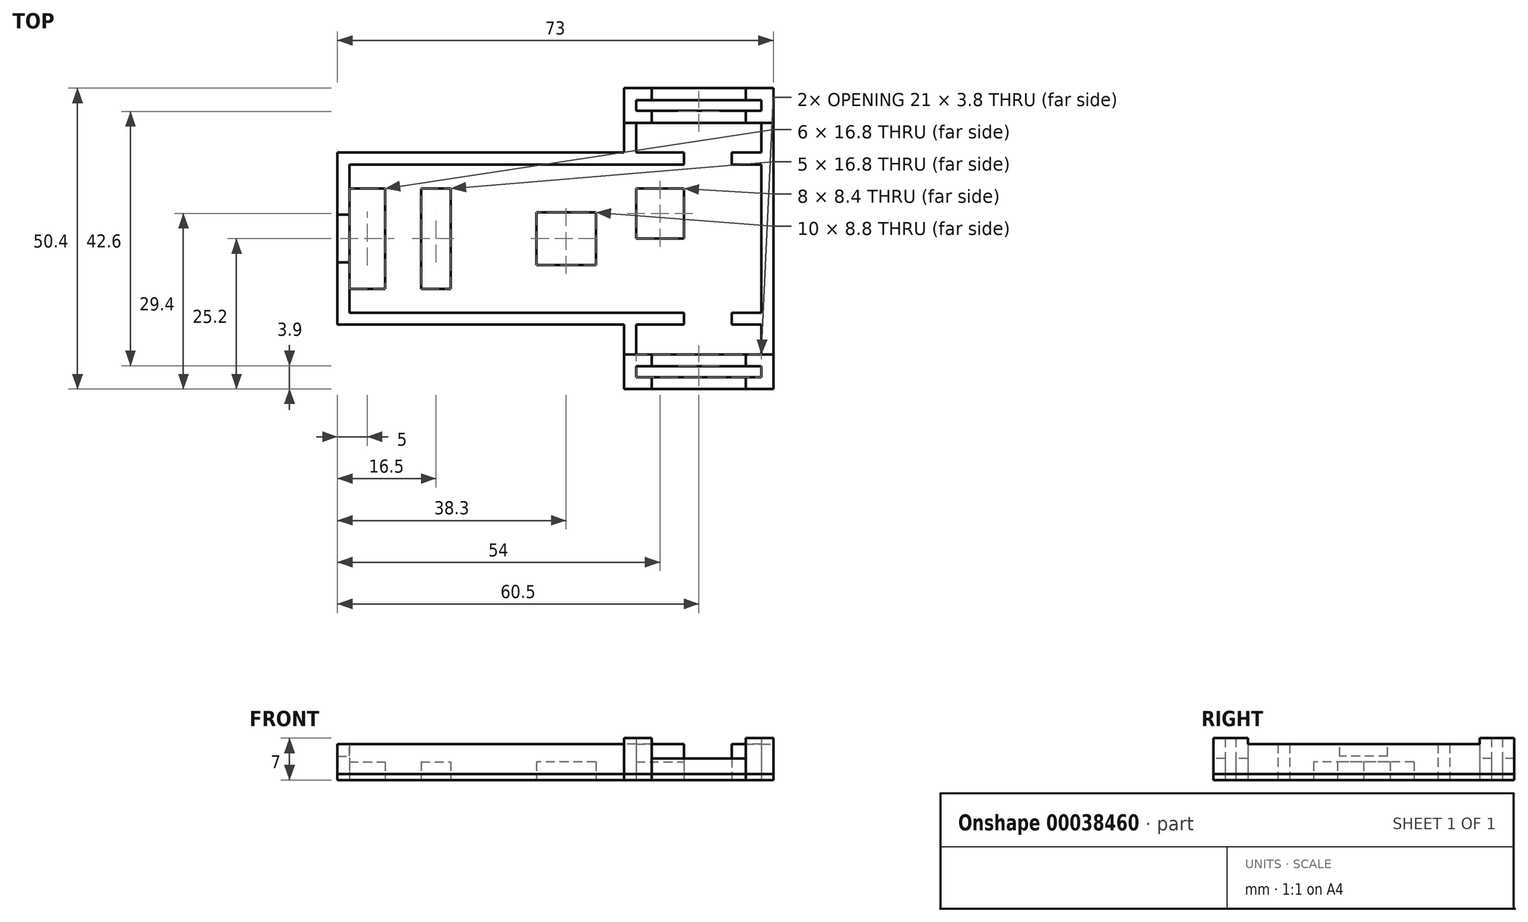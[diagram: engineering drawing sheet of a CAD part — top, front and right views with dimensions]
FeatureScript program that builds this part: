
annotation { "Feature Type Name" : "Feature", "Feature Type Description" : "" }
export const myFeature = defineFeature(function(context is Context, id is Id, definition is map)
    precondition{}
    {
        {
            var Q0;
            Q0=qCreatedBy(makeId("Top.planeOp"),FACE);
            var sketch = newSketch(context, id + "F0", { "sketchPlane" : qUnion([Q0])});
            skLineSegment(sketch, "E0.bottom", {"start": v(0, 0) * mm, "end": v(69, 0) * mm, "construction": true});
            skLineSegment(sketch, "E0.top", {"start": v(0, 24.8) * mm, "end": v(69, 24.8) * mm, "construction": true});
            skLineSegment(sketch, "E0.left", {"start": v(0, 0) * mm, "end": v(0, 24.8) * mm, "construction": true});
            skLineSegment(sketch, "E0.right", {"start": v(69, 0) * mm, "end": v(69, 24.8) * mm, "construction": true});
            skLineSegment(sketch, "E1.bottom", {"start": v(-2, 26.8) * mm, "end": v(71, 26.8) * mm, "construction": true});
            skLineSegment(sketch, "E1.top", {"start": v(-2, -2) * mm, "end": v(71, -2) * mm, "construction": true});
            skLineSegment(sketch, "E1.left", {"start": v(-2, 26.8) * mm, "end": v(-2, -2) * mm, "construction": true});
            skLineSegment(sketch, "E1.right", {"start": v(71, 26.8) * mm, "end": v(71, -2) * mm, "construction": true});
            skLineSegment(sketch, "E2.bottom", {"start": v(71, 26.8) * mm, "end": v(46, 26.8) * mm, "construction": true});
            skLineSegment(sketch, "E2.top", {"start": v(71, 37.6) * mm, "end": v(46, 37.6) * mm, "construction": true});
            skLineSegment(sketch, "E2.left", {"start": v(71, 26.8) * mm, "end": v(71, 37.6) * mm, "construction": true});
            skLineSegment(sketch, "E2.right", {"start": v(46, 26.8) * mm, "end": v(46, 37.6) * mm, "construction": true});
            skLineSegment(sketch, "E3.bottom", {"start": v(69, 26.8) * mm, "end": v(48, 26.8) * mm, "construction": true});
            skLineSegment(sketch, "E3.top", {"start": v(69, 35.6) * mm, "end": v(48, 35.6) * mm, "construction": true});
            skLineSegment(sketch, "E3.left", {"start": v(69, 26.8) * mm, "end": v(69, 35.6) * mm, "construction": true});
            skLineSegment(sketch, "E3.right", {"start": v(48, 26.8) * mm, "end": v(48, 35.6) * mm, "construction": true});
            skLineSegment(sketch, "E4.bottom", {"start": v(71, -2) * mm, "end": v(46, -2) * mm, "construction": true});
            skLineSegment(sketch, "E4.top", {"start": v(71, -12.8) * mm, "end": v(46, -12.8) * mm, "construction": true});
            skLineSegment(sketch, "E4.left", {"start": v(71, -2) * mm, "end": v(71, -12.8) * mm, "construction": true});
            skLineSegment(sketch, "E4.right", {"start": v(46, -2) * mm, "end": v(46, -12.8) * mm, "construction": true});
            skLineSegment(sketch, "E5.bottom", {"start": v(69, -2) * mm, "end": v(48, -2) * mm, "construction": true});
            skLineSegment(sketch, "E5.top", {"start": v(69, -10.8) * mm, "end": v(48, -10.8) * mm, "construction": true});
            skLineSegment(sketch, "E5.left", {"start": v(69, -2) * mm, "end": v(69, -10.8) * mm, "construction": true});
            skLineSegment(sketch, "E5.right", {"start": v(48, -2) * mm, "end": v(48, -10.8) * mm, "construction": true});
            skLineSegment(sketch, "E6", {"start": v(48, 31.8) * mm, "end": v(69, 31.8) * mm, "construction": true});
            skLineSegment(sketch, "E7", {"start": v(48, 33.8) * mm, "end": v(69, 33.8) * mm, "construction": true});
            skLineSegment(sketch, "E8", {"start": v(48, -7) * mm, "end": v(69, -7) * mm, "construction": true});
            skLineSegment(sketch, "E9", {"start": v(48, -9) * mm, "end": v(69, -9) * mm, "construction": true});
            skLineSegment(sketch, "E10", {"start": v(64, 26.8) * mm, "end": v(64, -2) * mm, "construction": true});
            skLineSegment(sketch, "E11", {"start": v(56, 26.8) * mm, "end": v(56, -2) * mm, "construction": true});
            skLineSegment(sketch, "E12", {"start": v(0, 4) * mm, "end": v(64, 4) * mm, "construction": true});
            skLineSegment(sketch, "E13", {"start": v(0, 20.8) * mm, "end": v(56, 20.8) * mm, "construction": true});
            skLineSegment(sketch, "E14", {"start": v(41.3, 20.8) * mm, "end": v(41.3, 4) * mm, "construction": true});
            skLineSegment(sketch, "E15.bottom", {"start": v(41.3, 16.8) * mm, "end": v(31.3, 16.8) * mm});
            skLineSegment(sketch, "E15.top", {"start": v(41.3, 8) * mm, "end": v(31.3, 8) * mm});
            skLineSegment(sketch, "E15.left", {"start": v(41.3, 16.8) * mm, "end": v(41.3, 8) * mm});
            skLineSegment(sketch, "E15.right", {"start": v(31.3, 16.8) * mm, "end": v(31.3, 8) * mm});
            skLineSegment(sketch, "E16.bottom", {"start": v(0, 20.8) * mm, "end": v(6, 20.8) * mm});
            skLineSegment(sketch, "E16.top", {"start": v(0, 4) * mm, "end": v(6, 4) * mm});
            skLineSegment(sketch, "E16.left", {"start": v(0, 20.8) * mm, "end": v(0, 4) * mm});
            skLineSegment(sketch, "E16.right", {"start": v(6, 20.8) * mm, "end": v(6, 4) * mm});
            skLineSegment(sketch, "E17.bottom", {"start": v(12, 20.8) * mm, "end": v(17, 20.8) * mm});
            skLineSegment(sketch, "E17.top", {"start": v(12, 4) * mm, "end": v(17, 4) * mm});
            skLineSegment(sketch, "E17.left", {"start": v(12, 20.8) * mm, "end": v(12, 4) * mm});
            skLineSegment(sketch, "E17.right", {"start": v(17, 20.8) * mm, "end": v(17, 4) * mm});
            skLineSegment(sketch, "E18", {"start": v(50.6, 31.8) * mm, "end": v(50.6, 37.6) * mm, "construction": true});
            skLineSegment(sketch, "E19", {"start": v(66.4, 31.8) * mm, "end": v(66.4, 37.6) * mm, "construction": true});
            skLineSegment(sketch, "E20", {"start": v(50.6, -7) * mm, "end": v(50.6, -12.8) * mm, "construction": true});
            skLineSegment(sketch, "E21", {"start": v(66.4, -7) * mm, "end": v(66.4, -12.8) * mm, "construction": true});
            skLineSegment(sketch, "E22", {"start": v(-2, 26.8) * mm, "end": v(46, 26.8) * mm});
            skLineSegment(sketch, "E23", {"start": v(46, 26.8) * mm, "end": v(46, 37.6) * mm});
            skLineSegment(sketch, "E24", {"start": v(46, 37.6) * mm, "end": v(50.6, 37.6) * mm});
            skLineSegment(sketch, "E25", {"start": v(50.6, 37.6) * mm, "end": v(50.6, 35.6) * mm});
            skLineSegment(sketch, "E26", {"start": v(50.6, 35.6) * mm, "end": v(48, 35.6) * mm});
            skLineSegment(sketch, "E27", {"start": v(48, 33.8) * mm, "end": v(50.6, 33.8) * mm});
            skLineSegment(sketch, "E28", {"start": v(50.6, 33.8) * mm, "end": v(50.6, 31.8) * mm});
            skLineSegment(sketch, "E29", {"start": v(50.6, 31.8) * mm, "end": v(48, 31.8) * mm});
            skLineSegment(sketch, "E30", {"start": v(48, 26.8) * mm, "end": v(48, 31.8) * mm});
            skLineSegment(sketch, "E31", {"start": v(48, 26.8) * mm, "end": v(56, 26.8) * mm});
            skLineSegment(sketch, "E32", {"start": v(56, 26.8) * mm, "end": v(56, 24.8) * mm});
            skLineSegment(sketch, "E33", {"start": v(56, 24.8) * mm, "end": v(0, 24.8) * mm});
            skLineSegment(sketch, "E34", {"start": v(0, 24.8) * mm, "end": v(0, 0) * mm});
            skLineSegment(sketch, "E35", {"start": v(0, 0) * mm, "end": v(56, 0) * mm});
            skLineSegment(sketch, "E36", {"start": v(56, 0) * mm, "end": v(56, -2) * mm});
            skLineSegment(sketch, "E37", {"start": v(56, -2) * mm, "end": v(48, -2) * mm});
            skLineSegment(sketch, "E38", {"start": v(48, -2) * mm, "end": v(48, -7) * mm});
            skLineSegment(sketch, "E39", {"start": v(48, -7) * mm, "end": v(50.6, -7) * mm});
            skLineSegment(sketch, "E40", {"start": v(50.6, -7) * mm, "end": v(50.6, -9) * mm});
            skLineSegment(sketch, "E41", {"start": v(48, -9) * mm, "end": v(50.6, -9) * mm});
            skLineSegment(sketch, "E42", {"start": v(48, -9) * mm, "end": v(48, -10.8) * mm});
            skLineSegment(sketch, "E43", {"start": v(48, -10.8) * mm, "end": v(50.6, -10.8) * mm});
            skLineSegment(sketch, "E44", {"start": v(50.6, -10.8) * mm, "end": v(50.6, -12.8) * mm});
            skLineSegment(sketch, "E45", {"start": v(50.6, -12.8) * mm, "end": v(46, -12.8) * mm});
            skLineSegment(sketch, "E46", {"start": v(46, -12.8) * mm, "end": v(46, -2) * mm});
            skLineSegment(sketch, "E47", {"start": v(46, -2) * mm, "end": v(-2, -2) * mm});
            skLineSegment(sketch, "E48", {"start": v(-2, -2) * mm, "end": v(-2, 26.8) * mm});
            skLineSegment(sketch, "E49", {"start": v(64, 26.8) * mm, "end": v(69, 26.8) * mm});
            skLineSegment(sketch, "E50", {"start": v(69, 26.8) * mm, "end": v(69, 31.8) * mm});
            skLineSegment(sketch, "E51", {"start": v(69, 31.8) * mm, "end": v(66.4, 31.8) * mm});
            skLineSegment(sketch, "E52", {"start": v(66.4, 31.8) * mm, "end": v(66.4, 33.8) * mm});
            skLineSegment(sketch, "E53", {"start": v(66.4, 33.8) * mm, "end": v(69, 33.8) * mm});
            skLineSegment(sketch, "E54", {"start": v(69, 33.8) * mm, "end": v(69, 35.6) * mm});
            skLineSegment(sketch, "E55", {"start": v(69, 35.6) * mm, "end": v(66.4, 35.6) * mm});
            skLineSegment(sketch, "E56", {"start": v(66.4, 35.6) * mm, "end": v(66.4, 37.6) * mm});
            skLineSegment(sketch, "E57", {"start": v(66.4, 37.6) * mm, "end": v(71, 37.6) * mm});
            skLineSegment(sketch, "E58", {"start": v(71, 37.6) * mm, "end": v(71, -12.8) * mm});
            skLineSegment(sketch, "E59", {"start": v(71, -12.8) * mm, "end": v(66.4, -12.8) * mm});
            skLineSegment(sketch, "E60", {"start": v(66.4, -12.8) * mm, "end": v(66.4, -10.8) * mm});
            skLineSegment(sketch, "E61", {"start": v(66.4, -10.8) * mm, "end": v(69, -10.8) * mm});
            skLineSegment(sketch, "E62", {"start": v(69, -10.8) * mm, "end": v(69, -9) * mm});
            skLineSegment(sketch, "E63", {"start": v(69, -9) * mm, "end": v(66.4, -9) * mm});
            skLineSegment(sketch, "E64", {"start": v(66.4, -9) * mm, "end": v(66.4, -7) * mm});
            skLineSegment(sketch, "E65", {"start": v(66.4, -7) * mm, "end": v(69, -7) * mm});
            skLineSegment(sketch, "E66", {"start": v(69, -7) * mm, "end": v(69, -2) * mm});
            skLineSegment(sketch, "E67", {"start": v(69, -2) * mm, "end": v(64, -2) * mm});
            skLineSegment(sketch, "E68", {"start": v(64, -2) * mm, "end": v(64, 0) * mm});
            skLineSegment(sketch, "E69", {"start": v(64, 0) * mm, "end": v(69, 0) * mm});
            skLineSegment(sketch, "E70", {"start": v(69, 0) * mm, "end": v(69, 24.8) * mm});
            skLineSegment(sketch, "E71", {"start": v(69, 24.8) * mm, "end": v(64, 24.8) * mm});
            skLineSegment(sketch, "E72", {"start": v(64, 24.8) * mm, "end": v(64, 26.8) * mm});
            skLineSegment(sketch, "E73", {"start": v(50.6, 37.6) * mm, "end": v(50.6, 35.6) * mm, "construction": true});
            skLineSegment(sketch, "E74", {"start": v(48, 35.6) * mm, "end": v(48, 33.8) * mm});
            skLineSegment(sketch, "E75", {"start": v(50.6, 37.6) * mm, "end": v(66.4, 37.6) * mm});
            skLineSegment(sketch, "E76", {"start": v(50.6, 35.6) * mm, "end": v(66.4, 35.6) * mm});
            skLineSegment(sketch, "E77", {"start": v(50.6, 33.8) * mm, "end": v(66.4, 33.8) * mm});
            skLineSegment(sketch, "E78", {"start": v(50.6, 31.8) * mm, "end": v(66.4, 31.8) * mm});
            skLineSegment(sketch, "E79", {"start": v(50.6, -7) * mm, "end": v(66.4, -7) * mm});
            skLineSegment(sketch, "E80", {"start": v(50.6, -9) * mm, "end": v(66.4, -9) * mm});
            skLineSegment(sketch, "E81", {"start": v(50.6, -10.8) * mm, "end": v(66.4, -10.8) * mm});
            skLineSegment(sketch, "E82", {"start": v(50.6, -12.8) * mm, "end": v(66.4, -12.8) * mm});
            skLineSegment(sketch, "E83.bottom", {"start": v(48, 20.8) * mm, "end": v(56, 20.8) * mm});
            skLineSegment(sketch, "E83.top", {"start": v(48, 12.4) * mm, "end": v(56, 12.4) * mm});
            skLineSegment(sketch, "E83.left", {"start": v(48, 20.8) * mm, "end": v(48, 12.4) * mm});
            skLineSegment(sketch, "E83.right", {"start": v(56, 20.8) * mm, "end": v(56, 12.4) * mm});
            skSolve(sketch);
        }
        {
            var Q0;
            {var subQ0=sQuery(id+"F0.wireOp",EDGE,"E16.bottom");Q0=makeQuery(id+"F0.imprint","IMPRINT",FACE,{"disambiguationData":[TD([[makeQuery(id+"F0.imprint","IMPRINT",EDGE,{"derivedFrom":subQ0}),-1.0]])]});}
            var Q1;
            Q1=makeQuery(id+"F0.imprint","IMPRINT",FACE,{"disambiguationData":[TD([[makeQuery(id+"F0.imprint","IMPRINT",EDGE,{"derivedFrom":sQuery(id+"F0.wireOp",EDGE,"E17.bottom")}),-1.0]])]});
            var Q2;
            Q2=makeQuery(id+"F0.imprint","IMPRINT",FACE,{"disambiguationData":[TD([[makeQuery(id+"F0.imprint","IMPRINT",EDGE,{"derivedFrom":sQuery(id+"F0.wireOp",EDGE,"E15.bottom")}),1.0]])]});
            var Q3;
            Q3=makeQuery(id+"F0.imprint","IMPRINT",FACE,{"disambiguationData":[TD([[makeQuery(id+"F0.imprint","IMPRINT",EDGE,{"derivedFrom":sQuery(id+"F0.wireOp",EDGE,"45062b85-0d93-40b0-8bcf-c9440ba23c84.bottom")}),1.0]])]});
            var Q4;
            Q4=makeQuery(id+"F0.imprint","IMPRINT",FACE,{"disambiguationData":[TD([[makeQuery(id+"F0.imprint","IMPRINT",EDGE,{"derivedFrom":sQuery(id+"F0.wireOp",EDGE,"E83.bottom")}),-1.0]])]});
            extrude(context, id + "F1", {"entities" : qUnion([Q0, Q1, Q2, Q3, Q4]), "depth" : 3 * mm});
        }
        {
            var Q0;
            Q0=makeQuery(id+"F0.imprint","IMPRINT",FACE,{"disambiguationData":[TD([[makeQuery(id+"F0.imprint","IMPRINT",EDGE,{"derivedFrom":sQuery(id+"F0.wireOp",EDGE,"E22")}),-1.0]])]});
            var Q1;
            Q1=makeQuery(id+"F0.imprint","IMPRINT",FACE,{"disambiguationData":[TD([[makeQuery(id+"F0.imprint","IMPRINT",EDGE,{"derivedFrom":sQuery(id+"F0.wireOp",EDGE,"E49")}),-1.0]])]});
            extrude(context, id + "F2", {"entities" : qUnion([Q0, Q1]), "operationType" : NewBodyOperationType.ADD, "depth" : 6 * mm});
        }
        {
            var Q0;
            Q0=makeQuery(id+"F0.imprint","IMPRINT",FACE,{"disambiguationData":[TD([[makeQuery(id+"F0.imprint","IMPRINT",EDGE,{"derivedFrom":sQuery(id+"F0.wireOp",EDGE,"E25")}),1.0]])]});
            var Q1;
            Q1=makeQuery(id+"F0.imprint","IMPRINT",FACE,{"disambiguationData":[TD([[makeQuery(id+"F0.imprint","IMPRINT",EDGE,{"derivedFrom":sQuery(id+"F0.wireOp",EDGE,"E28")}),1.0]])]});
            var Q2;
            Q2=makeQuery(id+"F0.imprint","IMPRINT",FACE,{"disambiguationData":[TD([[makeQuery(id+"F0.imprint","IMPRINT",EDGE,{"derivedFrom":sQuery(id+"F0.wireOp",EDGE,"E40")}),1.0]])]});
            var Q3;
            Q3=makeQuery(id+"F0.imprint","IMPRINT",FACE,{"disambiguationData":[TD([[makeQuery(id+"F0.imprint","IMPRINT",EDGE,{"derivedFrom":sQuery(id+"F0.wireOp",EDGE,"E44")}),1.0]])]});
            extrude(context, id + "F3", {"entities" : qUnion([Q0, Q1, Q2, Q3]), "depth" : 3.6 * mm});
        }
        {
            var Q0;
            Q0=makeQuery(id+"F0.imprint","IMPRINT",FACE,{"disambiguationData":[TD([[makeQuery(id+"F0.imprint","IMPRINT",EDGE,{"derivedFrom":sQuery(id+"F0.wireOp",EDGE,"45062b85-0d93-40b0-8bcf-c9440ba23c84.bottom")}),-1.0]])]});
            var Q1;
            Q1=makeQuery(id+"F0.imprint","IMPRINT",FACE,{"disambiguationData":[TD([[makeQuery(id+"F0.imprint","IMPRINT",EDGE,{"derivedFrom":sQuery(id+"F0.wireOp",EDGE,"E26")}),1.0]])]});
            var Q2;
            Q2=makeQuery(id+"F0.imprint","IMPRINT",FACE,{"disambiguationData":[TD([[makeQuery(id+"F0.imprint","IMPRINT",EDGE,{"derivedFrom":sQuery(id+"F0.wireOp",EDGE,"E41")}),-1.0]])]});
            extrude(context, id + "F4", {"entities" : qUnion([Q0, Q1, Q2]), "depth" : 1 * mm});
        }
        {
            var Q0;
            Q0=makeQuery(id+"F2.opExtrude","CAP_FACE",FACE,{"disambiguationData":[OSD([sQuery(id+"F0.wireOp",EDGE,"E22"),sQuery(id+"F0.wireOp",EDGE,"E23"),sQuery(id+"F0.wireOp",EDGE,"E24"),sQuery(id+"F0.wireOp",EDGE,"E25"),sQuery(id+"F0.wireOp",EDGE,"E26"),sQuery(id+"F0.wireOp",EDGE,"E27"),sQuery(id+"F0.wireOp",EDGE,"E28"),sQuery(id+"F0.wireOp",EDGE,"E29"),sQuery(id+"F0.wireOp",EDGE,"E30"),sQuery(id+"F0.wireOp",EDGE,"E31"),sQuery(id+"F0.wireOp",EDGE,"E32"),sQuery(id+"F0.wireOp",EDGE,"E33"),sQuery(id+"F0.wireOp",EDGE,"E34"),sQuery(id+"F0.wireOp",EDGE,"E35"),sQuery(id+"F0.wireOp",EDGE,"E36"),sQuery(id+"F0.wireOp",EDGE,"E37"),sQuery(id+"F0.wireOp",EDGE,"E38"),sQuery(id+"F0.wireOp",EDGE,"E39"),sQuery(id+"F0.wireOp",EDGE,"E40"),sQuery(id+"F0.wireOp",EDGE,"E41"),sQuery(id+"F0.wireOp",EDGE,"E42"),sQuery(id+"F0.wireOp",EDGE,"E43"),sQuery(id+"F0.wireOp",EDGE,"E44"),sQuery(id+"F0.wireOp",EDGE,"E45"),sQuery(id+"F0.wireOp",EDGE,"E46"),sQuery(id+"F0.wireOp",EDGE,"E47"),sQuery(id+"F0.wireOp",EDGE,"E48"),sQuery(id+"F0.wireOp",EDGE,"E74")])],"isStart":false});
            var sketch = newSketch(context, id + "F5", { "sketchPlane" : qUnion([Q0])});
            skLineSegment(sketch, "E84", {"start": v(50.6, 31.8) * mm, "end": v(46, 31.8) * mm});
            skPoint(sketch, "E84.endSnap0", {"position": v(49.3, 31.8) * mm});
            skLineSegment(sketch, "E85", {"start": v(46, 31.8) * mm, "end": v(46, 37.6) * mm});
            skLineSegment(sketch, "E86", {"start": v(46, 37.6) * mm, "end": v(50.6, 37.6) * mm});
            skLineSegment(sketch, "E87", {"start": v(50.6, 37.6) * mm, "end": v(50.6, 35.6) * mm});
            skLineSegment(sketch, "E88", {"start": v(50.6, 35.6) * mm, "end": v(48, 35.6) * mm});
            skLineSegment(sketch, "E89", {"start": v(48, 35.6) * mm, "end": v(48, 33.8) * mm});
            skLineSegment(sketch, "E90", {"start": v(48, 33.8) * mm, "end": v(50.6, 33.8) * mm});
            skLineSegment(sketch, "E91", {"start": v(50.6, 33.8) * mm, "end": v(50.6, 31.8) * mm});
            skLineSegment(sketch, "E92", {"start": v(50.6, -7) * mm, "end": v(46, -7) * mm});
            skLineSegment(sketch, "E93", {"start": v(46, -7) * mm, "end": v(46, -12.8) * mm});
            skLineSegment(sketch, "E94", {"start": v(46, -12.8) * mm, "end": v(50.6, -12.8) * mm});
            skLineSegment(sketch, "E95", {"start": v(50.6, -12.8) * mm, "end": v(50.6, -10.8) * mm});
            skLineSegment(sketch, "E96", {"start": v(50.6, -10.8) * mm, "end": v(48, -10.8) * mm});
            skLineSegment(sketch, "E97", {"start": v(48, -10.8) * mm, "end": v(48, -9) * mm});
            skLineSegment(sketch, "E98", {"start": v(48, -9) * mm, "end": v(50.6, -9) * mm});
            skLineSegment(sketch, "E99", {"start": v(50.6, -9) * mm, "end": v(50.6, -7) * mm});
            skSolve(sketch);
        }
        {
            var Q0;
            Q0=makeQuery(id+"F2.opExtrude","CAP_FACE",FACE,{"disambiguationData":[OSD([sQuery(id+"F0.wireOp",EDGE,"E49"),sQuery(id+"F0.wireOp",EDGE,"E50"),sQuery(id+"F0.wireOp",EDGE,"E51"),sQuery(id+"F0.wireOp",EDGE,"E52"),sQuery(id+"F0.wireOp",EDGE,"E53"),sQuery(id+"F0.wireOp",EDGE,"E54"),sQuery(id+"F0.wireOp",EDGE,"E55"),sQuery(id+"F0.wireOp",EDGE,"E56"),sQuery(id+"F0.wireOp",EDGE,"E57"),sQuery(id+"F0.wireOp",EDGE,"E58"),sQuery(id+"F0.wireOp",EDGE,"E59"),sQuery(id+"F0.wireOp",EDGE,"E60"),sQuery(id+"F0.wireOp",EDGE,"E61"),sQuery(id+"F0.wireOp",EDGE,"E62"),sQuery(id+"F0.wireOp",EDGE,"E63"),sQuery(id+"F0.wireOp",EDGE,"E64"),sQuery(id+"F0.wireOp",EDGE,"E65"),sQuery(id+"F0.wireOp",EDGE,"E66"),sQuery(id+"F0.wireOp",EDGE,"E67"),sQuery(id+"F0.wireOp",EDGE,"E68"),sQuery(id+"F0.wireOp",EDGE,"E69"),sQuery(id+"F0.wireOp",EDGE,"E70"),sQuery(id+"F0.wireOp",EDGE,"E71"),sQuery(id+"F0.wireOp",EDGE,"E72")])],"isStart":false});
            var sketch = newSketch(context, id + "F6", { "sketchPlane" : qUnion([Q0])});
            skLineSegment(sketch, "E100", {"start": v(66.4, 31.8) * mm, "end": v(71, 31.8) * mm});
            skLineSegment(sketch, "E101", {"start": v(71, 31.8) * mm, "end": v(71, 37.6) * mm});
            skLineSegment(sketch, "E102", {"start": v(71, 37.6) * mm, "end": v(66.4, 37.6) * mm});
            skLineSegment(sketch, "E103", {"start": v(66.4, 37.6) * mm, "end": v(66.4, 35.6) * mm});
            skLineSegment(sketch, "E104", {"start": v(66.4, 35.6) * mm, "end": v(69, 35.6) * mm});
            skLineSegment(sketch, "E105", {"start": v(69, 35.6) * mm, "end": v(69, 33.8) * mm});
            skLineSegment(sketch, "E106", {"start": v(69, 33.8) * mm, "end": v(66.4, 33.8) * mm});
            skLineSegment(sketch, "E107", {"start": v(66.4, 33.8) * mm, "end": v(66.4, 31.8) * mm});
            skLineSegment(sketch, "E108", {"start": v(66.4, -7) * mm, "end": v(71, -7) * mm});
            skLineSegment(sketch, "E109", {"start": v(71, -7) * mm, "end": v(71, -12.8) * mm});
            skLineSegment(sketch, "E110", {"start": v(71, -12.8) * mm, "end": v(66.4, -12.8) * mm});
            skLineSegment(sketch, "E111", {"start": v(66.4, -12.8) * mm, "end": v(66.4, -10.8) * mm});
            skLineSegment(sketch, "E112", {"start": v(66.4, -10.8) * mm, "end": v(69, -10.8) * mm});
            skLineSegment(sketch, "E113", {"start": v(69, -10.8) * mm, "end": v(69, -9) * mm});
            skLineSegment(sketch, "E114", {"start": v(69, -9) * mm, "end": v(66.4, -9) * mm});
            skLineSegment(sketch, "E115", {"start": v(66.4, -9) * mm, "end": v(66.4, -7) * mm});
            skSolve(sketch);
        }
        {
            var Q0;
            {var subQ2=sQuery(id+"F5.wireOp",EDGE,"E85");Q0=makeQuery(id+"F5.imprint","IMPRINT",FACE,{"disambiguationData":[TD([[makeQuery(id+"F5.imprint","IMPRINT",EDGE,{"derivedFrom":subQ2}),-1.0]])]});}
            var Q1;
            {var subQ0=sQuery(id+"F6.wireOp",EDGE,"E101");Q1=makeQuery(id+"F6.imprint","IMPRINT",FACE,{"disambiguationData":[TD([[makeQuery(id+"F6.imprint","IMPRINT",EDGE,{"derivedFrom":subQ0}),-1.0]])]});}
            var Q2;
            {var subQ0=sQuery(id+"F6.wireOp",EDGE,"E109");Q2=makeQuery(id+"F6.imprint","IMPRINT",FACE,{"disambiguationData":[TD([[makeQuery(id+"F6.imprint","IMPRINT",EDGE,{"derivedFrom":subQ0}),-1.0]])]});}
            var Q3;
            {var subQ3=sQuery(id+"F5.wireOp",EDGE,"E93");Q3=makeQuery(id+"F5.imprint","IMPRINT",FACE,{"disambiguationData":[TD([[makeQuery(id+"F5.imprint","IMPRINT",EDGE,{"derivedFrom":subQ3}),-1.0]])]});}
            extrude(context, id + "F7", {"entities" : qUnion([Q0, Q1, Q2, Q3]), "operationType" : NewBodyOperationType.ADD, "depth" : 1 * mm});
        }
        {
            var Q0;
            Q0 = qSketchRegion(id + "F0", true);
            var Q1;
            Q1=makeQuery(id+"F0.imprint","IMPRINT",FACE,{"disambiguationData":[TD([[makeQuery(id+"F0.imprint","IMPRINT",EDGE,{"derivedFrom":sQuery(id+"F0.wireOp",EDGE,"E15.bottom")}),-1.0]])]});
            extrude(context, id + "F8", {"entities" : qUnion([Q0, Q1]), "depth" : 1 * mm});
        }
        {
            var Q0;
            Q0=makeQuery(id+"F2.opExtrude","CAP_FACE",FACE,{"disambiguationData":[OSD([sQuery(id+"F0.wireOp",EDGE,"E22"),sQuery(id+"F0.wireOp",EDGE,"E23"),sQuery(id+"F0.wireOp",EDGE,"E24"),sQuery(id+"F0.wireOp",EDGE,"E25"),sQuery(id+"F0.wireOp",EDGE,"E26"),sQuery(id+"F0.wireOp",EDGE,"E27"),sQuery(id+"F0.wireOp",EDGE,"E28"),sQuery(id+"F0.wireOp",EDGE,"E29"),sQuery(id+"F0.wireOp",EDGE,"E30"),sQuery(id+"F0.wireOp",EDGE,"E31"),sQuery(id+"F0.wireOp",EDGE,"E32"),sQuery(id+"F0.wireOp",EDGE,"E33"),sQuery(id+"F0.wireOp",EDGE,"E34"),sQuery(id+"F0.wireOp",EDGE,"E35"),sQuery(id+"F0.wireOp",EDGE,"E36"),sQuery(id+"F0.wireOp",EDGE,"E37"),sQuery(id+"F0.wireOp",EDGE,"E38"),sQuery(id+"F0.wireOp",EDGE,"E39"),sQuery(id+"F0.wireOp",EDGE,"E40"),sQuery(id+"F0.wireOp",EDGE,"E41"),sQuery(id+"F0.wireOp",EDGE,"E42"),sQuery(id+"F0.wireOp",EDGE,"E43"),sQuery(id+"F0.wireOp",EDGE,"E44"),sQuery(id+"F0.wireOp",EDGE,"E45"),sQuery(id+"F0.wireOp",EDGE,"E46"),sQuery(id+"F0.wireOp",EDGE,"E47"),sQuery(id+"F0.wireOp",EDGE,"E48"),sQuery(id+"F0.wireOp",EDGE,"E74")])],"isStart":false});
            var sketch = newSketch(context, id + "F9", { "sketchPlane" : qUnion([Q0])});
            skLineSegment(sketch, "E116", {"start": v(-2, 12.4) * mm, "end": v(0, 12.4) * mm, "construction": true});
            skLineSegment(sketch, "E117.bottom", {"start": v(-2, 16.4) * mm, "end": v(0, 16.4) * mm});
            skLineSegment(sketch, "E117.top", {"start": v(-2, 8.4) * mm, "end": v(0, 8.4) * mm});
            skLineSegment(sketch, "E117.left", {"start": v(-2, 16.4) * mm, "end": v(-2, 8.4) * mm});
            skLineSegment(sketch, "E117.right", {"start": v(0, 16.4) * mm, "end": v(0, 8.4) * mm});
            skSolve(sketch);
        }
        {
            var Q0;
            Q0 = qSketchRegion(id + "F9", true);
            extrude(context, id + "F10", {"entities" : qUnion([Q0]), "operationType" : NewBodyOperationType.REMOVE, "oppositeDirection" : true, "depth" : 2 * mm});
        }
    });
